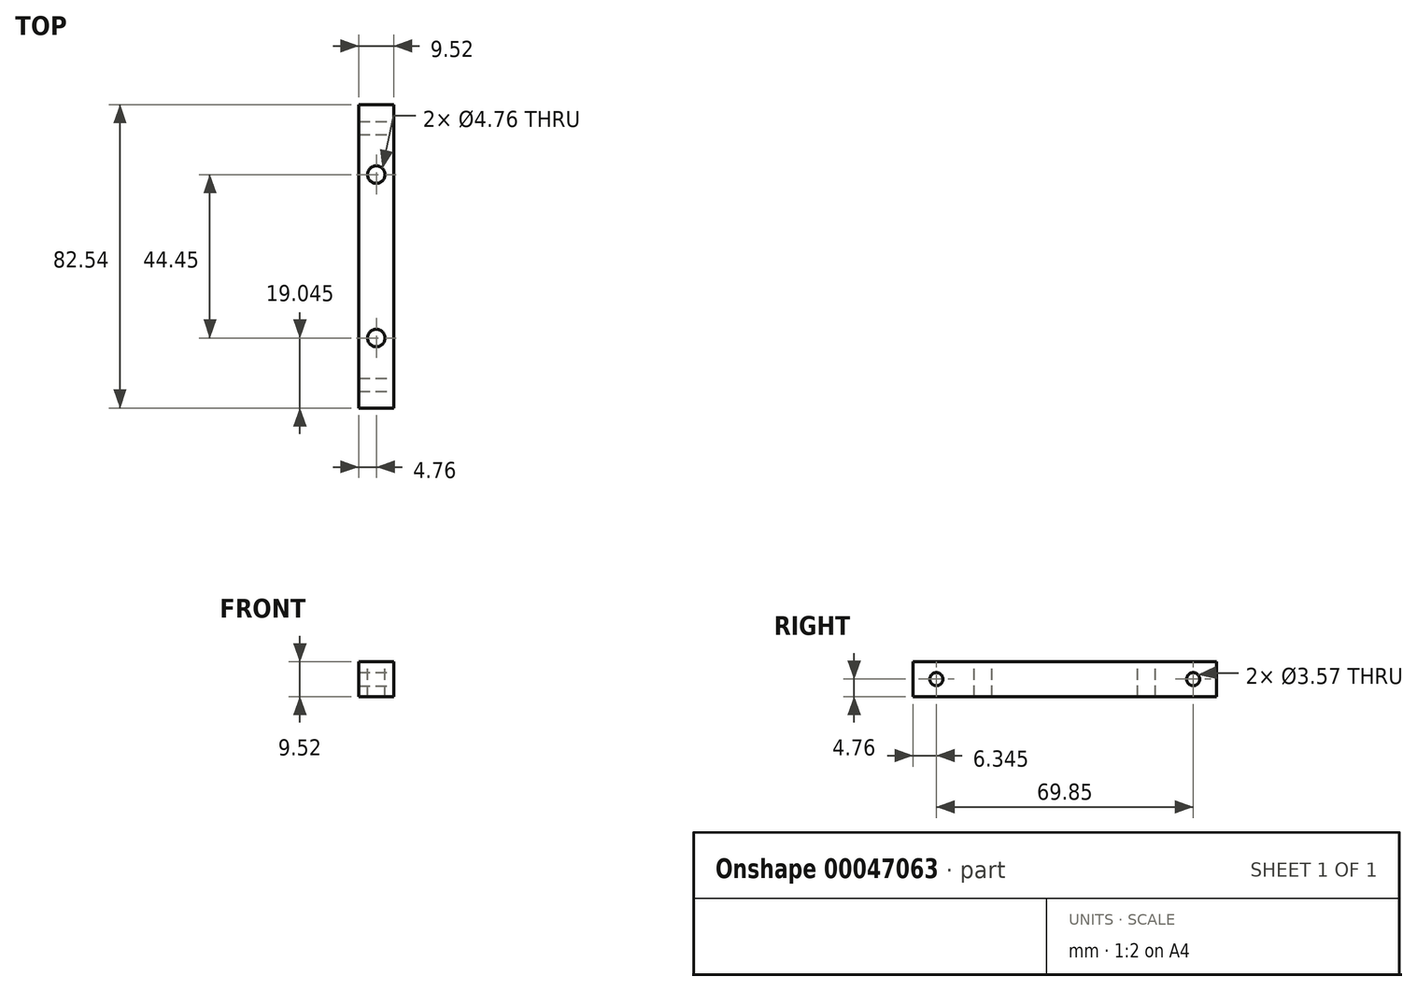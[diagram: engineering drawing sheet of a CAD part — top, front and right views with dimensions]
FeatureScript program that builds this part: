
annotation { "Feature Type Name" : "Feature", "Feature Type Description" : "" }
export const myFeature = defineFeature(function(context is Context, id is Id, definition is map)
    precondition{}
    {
        {
            var Q0;
            Q0=qCreatedBy(makeId("Front.planeOp"),FACE);
            var sketch = newSketch(context, id + "F0", { "sketchPlane" : qUnion([Q0])});
            skLineSegment(sketch, "E0.rect.bottom", {"start": v(4.76, 4.76) * mm, "end": v(-4.76, 4.76) * mm});
            skLineSegment(sketch, "E0.rect.top", {"start": v(4.76, -4.76) * mm, "end": v(-4.76, -4.76) * mm});
            skLineSegment(sketch, "E0.rect.left", {"start": v(4.76, 4.76) * mm, "end": v(4.76, -4.76) * mm});
            skLineSegment(sketch, "E0.rect.right", {"start": v(-4.76, 4.76) * mm, "end": v(-4.76, -4.76) * mm});
            skPoint(sketch, "E0.rect.middle", {"position": v(0, 0) * mm});
            skSolve(sketch);
        }
        {
            var Q0;
            Q0 = qSketchRegion(id + "F0", true);
            extrude(context, id + "F1", {"entities" : qUnion([Q0]), "endBound" : BoundingType.SYMMETRIC, "depth" : 82.55 * mm});
        }
        {
            var Q0;
            Q0=makeQuery(id+"F1.opExtrude","SWEPT_FACE",FACE,{"disambiguationData":[OSD([sQuery(id+"F0.wireOp",EDGE,"E0.rect.bottom")])]});
            var sketch = newSketch(context, id + "F2", { "sketchPlane" : qUnion([Q0])});
            skCircle(sketch, "E1", {"center": v(0, 22.23) * mm, "radius": 2.38 * mm});
            skCircle(sketch, "E2.MirrorC", {"center": v(0, -22.23) * mm, "radius": 2.38 * mm});
            skSolve(sketch);
        }
        {
            var Q0;
            Q0 = qSketchRegion(id + "F2", true);
            var Q1;
            Q1=makeQuery(id+"F1.opExtrude","SWEPT_FACE",FACE,{"disambiguationData":[OSD([sQuery(id+"F0.wireOp",EDGE,"E0.rect.top")])]});
            extrude(context, id + "F3", {"entities" : qUnion([Q0]), "operationType" : NewBodyOperationType.REMOVE, "endBound" : BoundingType.UP_TO_SURFACE, "oppositeDirection" : true, "endBoundEntityFace" : qUnion([Q1]), "depth" : 25.4 * mm});
        }
        {
            var Q0;
            Q0=makeQuery(id+"F1.opExtrude","SWEPT_FACE",FACE,{"disambiguationData":[OSD([sQuery(id+"F0.wireOp",EDGE,"E0.rect.left")])]});
            var sketch = newSketch(context, id + "F4", { "sketchPlane" : qUnion([Q0])});
            skCircle(sketch, "E3", {"center": v(-34.93, 0) * mm, "radius": 1.79 * mm});
            skCircle(sketch, "E4.MirrorC", {"center": v(34.93, 0) * mm, "radius": 1.79 * mm});
            skSolve(sketch);
        }
        {
            var Q0;
            Q0 = qSketchRegion(id + "F4", true);
            var Q1;
            Q1=makeQuery(id+"F1.opExtrude","SWEPT_FACE",FACE,{"disambiguationData":[OSD([sQuery(id+"F0.wireOp",EDGE,"E0.rect.right")])]});
            extrude(context, id + "F5", {"entities" : qUnion([Q0]), "operationType" : NewBodyOperationType.REMOVE, "endBound" : BoundingType.UP_TO_SURFACE, "oppositeDirection" : true, "endBoundEntityFace" : qUnion([Q1]), "depth" : 25.4 * mm});
        }
    });
